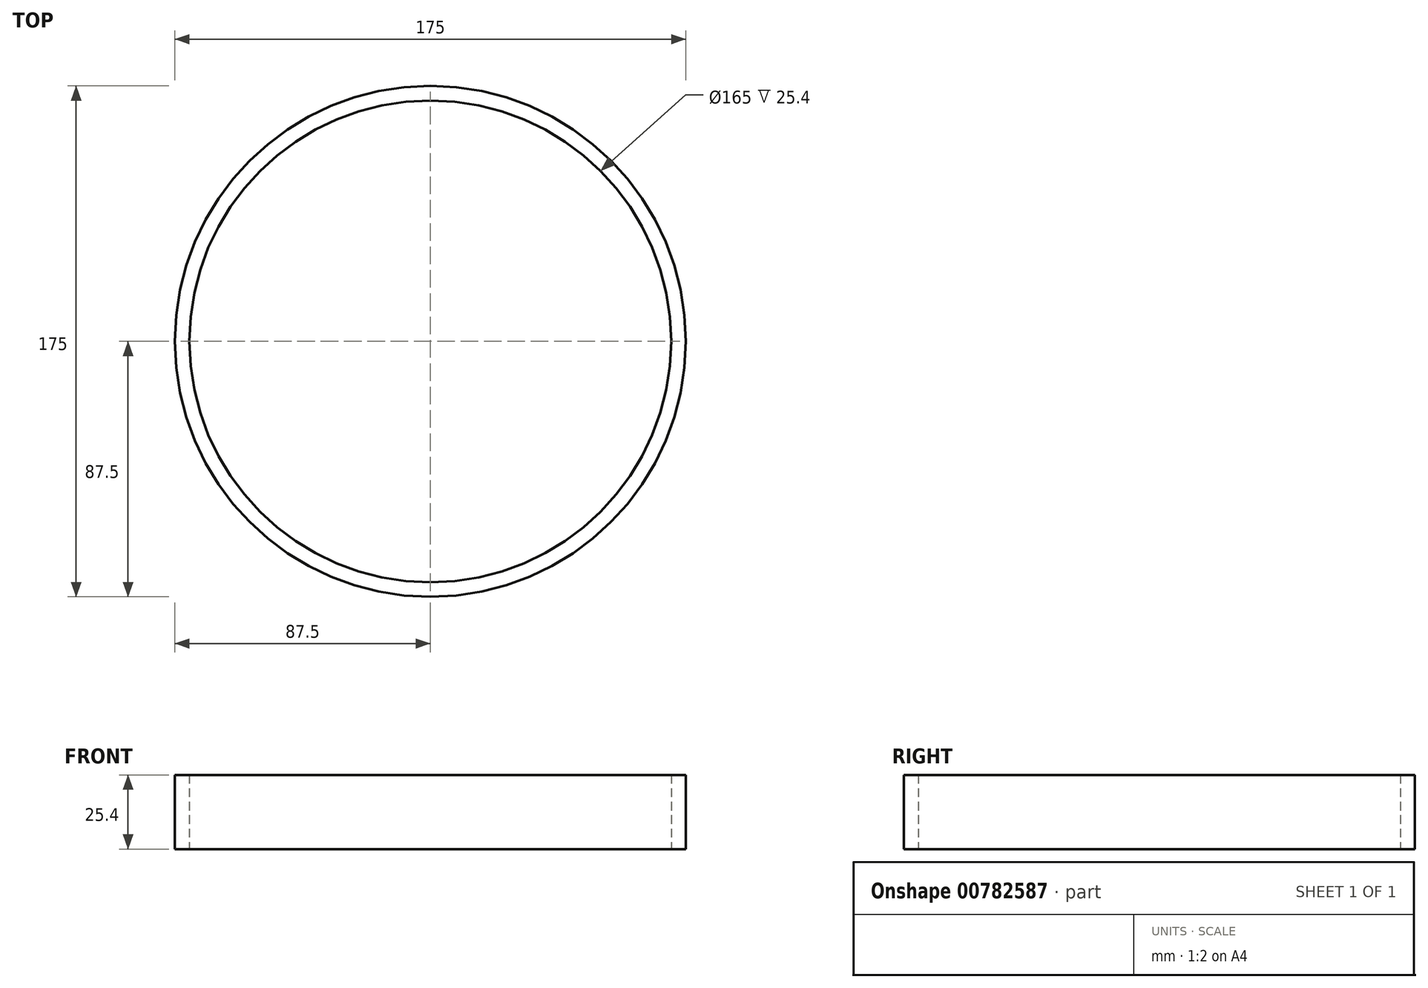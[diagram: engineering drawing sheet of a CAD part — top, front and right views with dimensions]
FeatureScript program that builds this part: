
annotation { "Feature Type Name" : "Feature", "Feature Type Description" : "" }
export const myFeature = defineFeature(function(context is Context, id is Id, definition is map)
    precondition{}
    {
        {
            var Q0;
            Q0=qCreatedBy(makeId("Top.planeOp"),FACE);
            var sketch = newSketch(context, id + "F0", { "sketchPlane" : qUnion([Q0])});
            skCircle(sketch, "E0", {"center": v(0, 0) * mm, "radius": 87.5 * mm});
            skCircle(sketch, "E1", {"center": v(0, 0) * mm, "radius": 82.5 * mm});
            skSolve(sketch);
        }
        {
            var Q0;
            Q0 = qSketchRegion(id + "F0", true);
            extrude(context, id + "F1", {"entities" : qUnion([Q0]), "depth" : 25.4 * mm, "offsetDistance" : 25.4 * mm});
        }
    });
